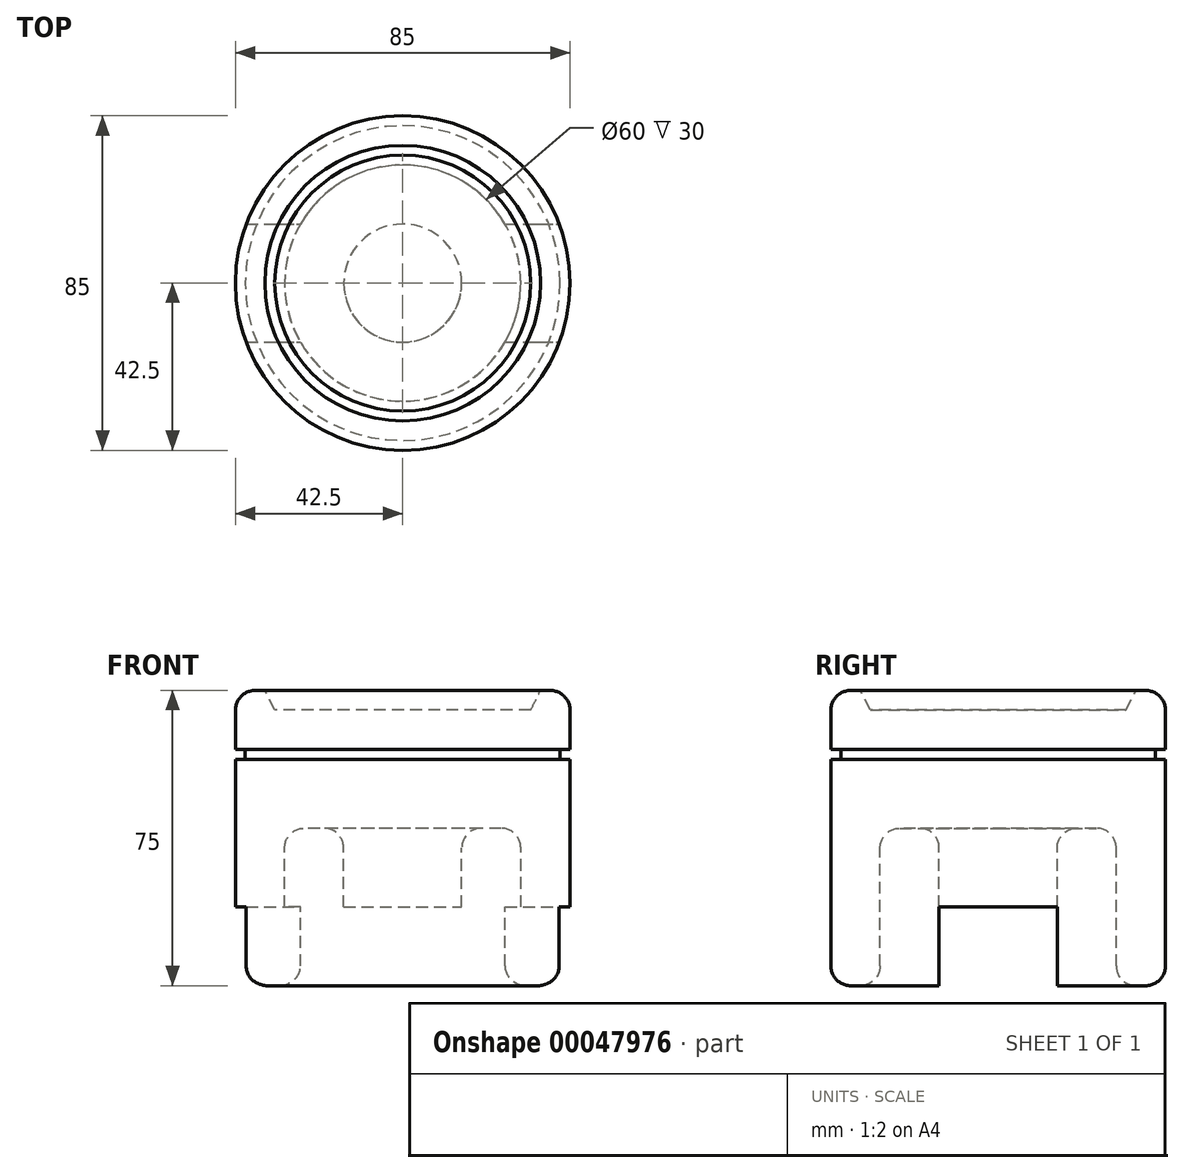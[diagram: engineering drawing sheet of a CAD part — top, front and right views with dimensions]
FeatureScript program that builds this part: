
annotation { "Feature Type Name" : "Feature", "Feature Type Description" : "" }
export const myFeature = defineFeature(function(context is Context, id is Id, definition is map)
    precondition{}
    {
        {
            var Q0;
            Q0=qCreatedBy(makeId("Front.planeOp"),FACE);
            var sketch = newSketch(context, id + "F0", { "sketchPlane" : qUnion([Q0])});
            skLineSegment(sketch, "E0", {"start": v(-42.5, 5) * mm, "end": v(-42.5, 70) * mm});
            skLineSegment(sketch, "E1", {"start": v(-37.5, 75) * mm, "end": v(0, 75) * mm});
            skLineSegment(sketch, "E2", {"start": v(0, 75) * mm, "end": v(0, 0) * mm});
            skLineSegment(sketch, "E3", {"start": v(0, 0) * mm, "end": v(-10, 0) * mm});
            skLineSegment(sketch, "E4", {"start": v(-15, 5) * mm, "end": v(-15, 35) * mm});
            skLineSegment(sketch, "E5", {"start": v(-20, 40) * mm, "end": v(-25, 40) * mm});
            skLineSegment(sketch, "E6", {"start": v(-30, 35) * mm, "end": v(-30, 5) * mm});
            skLineSegment(sketch, "E7", {"start": v(-35, 0) * mm, "end": v(-37.5, 0) * mm});
            skPoint(sketch, "E8.visualSharp", {"position": v(-30, 40) * mm});
            skArc(sketch, "E8.filletArc", {"start": v(-25, 40) * mm, "mid": v(-28.54, 38.54) * mm, "end": v(-30, 35) * mm});
            skPoint(sketch, "E9.visualSharp", {"position": v(-15, 40) * mm});
            skArc(sketch, "E9.filletArc", {"start": v(-15, 35) * mm, "mid": v(-16.46, 38.54) * mm, "end": v(-20, 40) * mm});
            skPoint(sketch, "E10.visualSharp", {"position": v(-15, 0) * mm});
            skArc(sketch, "E10.filletArc", {"start": v(-15, 5) * mm, "mid": v(-13.54, 1.46) * mm, "end": v(-10, 0) * mm});
            skPoint(sketch, "E11.visualSharp", {"position": v(-30, 0) * mm});
            skArc(sketch, "E11.filletArc", {"start": v(-35, 0) * mm, "mid": v(-31.46, 1.46) * mm, "end": v(-30, 5) * mm});
            skPoint(sketch, "E12.visualSharp", {"position": v(-42.5, 0) * mm});
            skArc(sketch, "E12.filletArc", {"start": v(-42.5, 5) * mm, "mid": v(-41.04, 1.46) * mm, "end": v(-37.5, 0) * mm});
            skPoint(sketch, "E13.visualSharp", {"position": v(-42.5, 75) * mm});
            skArc(sketch, "E13.filletArc", {"start": v(-37.5, 75) * mm, "mid": v(-41.04, 73.54) * mm, "end": v(-42.5, 70) * mm});
            skSolve(sketch);
        }
        {
            var Q0;
            Q0 = qSketchRegion(id + "F0", true);
            var Q1;
            Q1=sQuery(id+"F0.wireOp",EDGE,"E2");
            revolve(context, id + "F1", {"entities" : qUnion([Q0]), "axis" : qUnion([Q1]), "revolveType" : RevolveType.FULL});
        }
        {
            var Q0;
            Q0=makeQuery(id+"F1.opRevolve","SWEPT_FACE",FACE,{"disambiguationData":[OSD([sQuery(id+"F0.wireOp",EDGE,"E3")])]});
            var sketch = newSketch(context, id + "F2", { "sketchPlane" : qUnion([Q0])});
            skLineSegment(sketch, "E14.bottom", {"start": v(-100, 15) * mm, "end": v(100, 15) * mm});
            skLineSegment(sketch, "E14.top", {"start": v(-100, -15) * mm, "end": v(100, -15) * mm});
            skLineSegment(sketch, "E14.left", {"start": v(-100, 15) * mm, "end": v(-100, -15) * mm});
            skLineSegment(sketch, "E14.right", {"start": v(100, 15) * mm, "end": v(100, -15) * mm});
            skSolve(sketch);
        }
        {
            var Q0;
            Q0 = qSketchRegion(id + "F2", true);
            extrude(context, id + "F3", {"entities" : qUnion([Q0]), "operationType" : NewBodyOperationType.REMOVE, "oppositeDirection" : true, "depth" : 20 * mm});
        }
        {
            var Q0;
            Q0=makeQuery(id+"F1.opRevolve","SWEPT_FACE",FACE,{"disambiguationData":[OSD([sQuery(id+"F0.wireOp",EDGE,"E1")])]});
            var sketch = newSketch(context, id + "F4", { "sketchPlane" : qUnion([Q0])});
            skCircle(sketch, "E15", {"center": v(0, 0) * mm, "radius": 35 * mm});
            skSolve(sketch);
        }
        {
            var Q0;
            Q0=makeQuery(id+"F4.imprint","IMPRINT",FACE,{"disambiguationData":[TD([[makeQuery(id+"F4.imprint","IMPRINT",EDGE,{"derivedFrom":sQuery(id+"F4.wireOp",EDGE,"E15")}),1.0]])]});
            cPlane(context, id + "F5", {"entities" : qUnion([Q0]), "cplaneType" : CPlaneType.OFFSET, "offset" : 5 * mm, "oppositeDirection" : true, "width" : 152.4 * mm, "height" : 152.4 * mm});
        }
        {
            var Q0;
            Q0=qCreatedBy(id+"F5.planeOp",FACE);
            var sketch = newSketch(context, id + "F6", { "sketchPlane" : qUnion([Q0])});
            skCircle(sketch, "E16", {"center": v(0, 0) * mm, "radius": 32.5 * mm});
            skSolve(sketch);
        }
        {
            var Q1;
            Q1 = qSketchRegion(id + "F6", true);
            var Q2;
            Q2 = qSketchRegion(id + "F4", true);
            loft(context, id + "F7", {"operationType" : NewBodyOperationType.REMOVE, "sheetProfilesArray" : [{ "sheetProfileEntities" : qUnion([Q1]) }, { "sheetProfileEntities" : qUnion([Q2]) }]});
        }
        {
            var Q0;
            Q0=makeQuery(id+"F3.boolean.opBoolean","COPY",FACE,{"disambiguationData":[OD(1.0)],"derivedFrom":makeQuery(id+"F3.opExtrude","SWEPT_FACE",FACE,{"disambiguationData":[OSD([sQuery(id+"F2.wireOp",EDGE,"E14.top")])]})});
            var sketch = newSketch(context, id + "F8", { "sketchPlane" : qUnion([Q0])});
            skLineSegment(sketch, "E17.bottom", {"start": v(42.5, 60) * mm, "end": v(40, 60) * mm});
            skLineSegment(sketch, "E17.top", {"start": v(42.5, 57.5) * mm, "end": v(40, 57.5) * mm});
            skLineSegment(sketch, "E17.left", {"start": v(42.5, 60) * mm, "end": v(42.5, 57.5) * mm});
            skLineSegment(sketch, "E17.right", {"start": v(40, 60) * mm, "end": v(40, 57.5) * mm});
            skSolve(sketch);
        }
        {
            var Q0;
            Q0=qCreatedBy(makeId("Front.planeOp"),FACE);
            var sketch = newSketch(context, id + "F9", { "sketchPlane" : qUnion([Q0])});
            skLineSegment(sketch, "E18.0", {"start": v(42.5, 60) * mm, "end": v(40, 60) * mm});
            skLineSegment(sketch, "E19.0", {"start": v(40, 60) * mm, "end": v(40, 57.5) * mm});
            skLineSegment(sketch, "E20.0", {"start": v(42.5, 57.5) * mm, "end": v(40, 57.5) * mm});
            skLineSegment(sketch, "E21.0", {"start": v(42.5, 60) * mm, "end": v(42.5, 57.5) * mm});
            skLineSegment(sketch, "E22", {"start": v(0, -24.28) * mm, "end": v(0, 112.35) * mm, "construction": true});
            skSolve(sketch);
        }
        {
            var Q0;
            Q0 = qSketchRegion(id + "F9", true);
            var Q1;
            Q1=sQuery(id+"F9.wireOp",EDGE,"E22");
            revolve(context, id + "F10", {"operationType" : NewBodyOperationType.REMOVE, "entities" : qUnion([Q0]), "axis" : qUnion([Q1]), "revolveType" : RevolveType.FULL, "oppositeDirection" : true});
        }
    });
